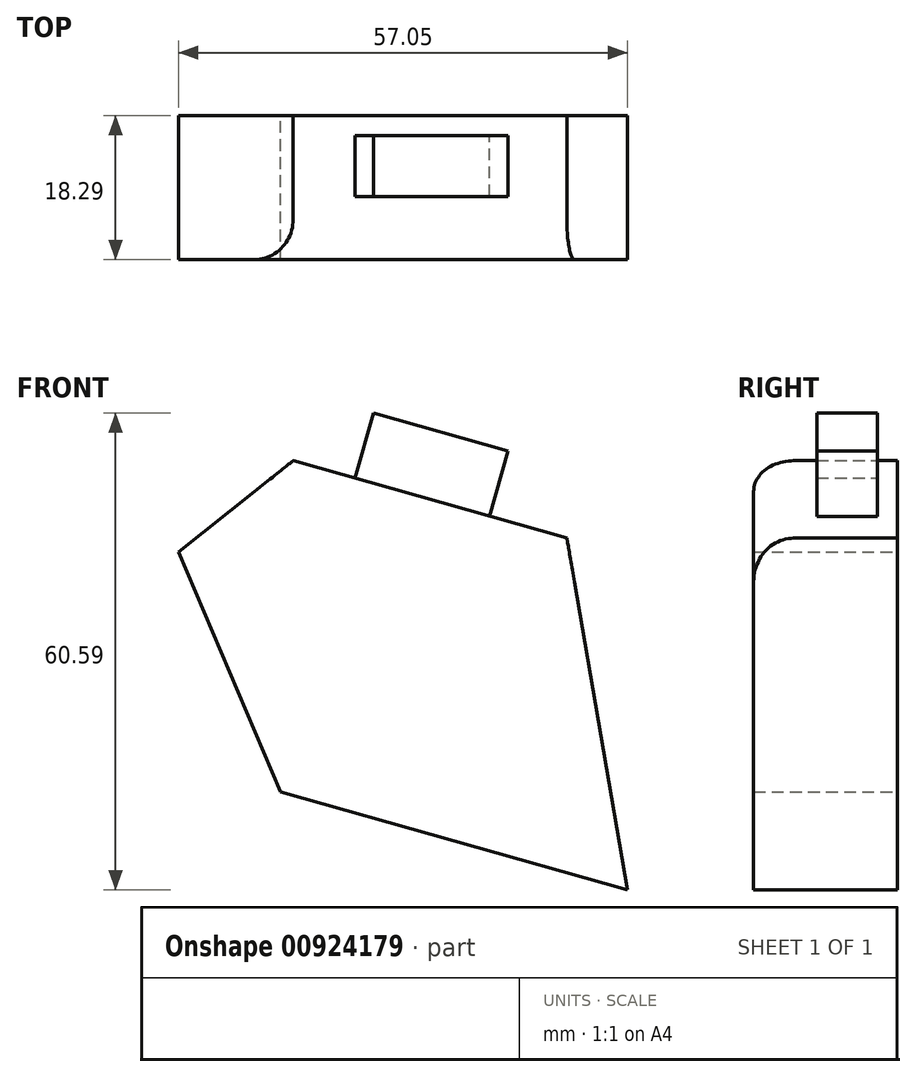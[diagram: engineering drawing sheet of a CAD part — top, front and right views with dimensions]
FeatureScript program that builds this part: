
annotation { "Feature Type Name" : "Feature", "Feature Type Description" : "" }
export const myFeature = defineFeature(function(context is Context, id is Id, definition is map)
    precondition{}
    {
        {
            var Q0;
            Q0=qCreatedBy(makeId("Front.planeOp"),FACE);
            var sketch = newSketch(context, id + "F0", { "sketchPlane" : qUnion([Q0])});
            skLineSegment(sketch, "E0", {"start": v(-28.41, 12.5) * mm, "end": v(-13.86, 24.09) * mm});
            skLineSegment(sketch, "E1", {"start": v(-13.86, 24.09) * mm, "end": v(20.9, 14.25) * mm});
            skLineSegment(sketch, "E2", {"start": v(20.9, 14.25) * mm, "end": v(28.64, -30.44) * mm});
            skLineSegment(sketch, "E3", {"start": v(28.64, -30.44) * mm, "end": v(-15.48, -17.96) * mm});
            skLineSegment(sketch, "E4", {"start": v(-15.48, -17.96) * mm, "end": v(-28.41, 12.5) * mm});
            skSolve(sketch);
        }
        {
            var Q0;
            Q0=makeQuery(id+"F0.imprint","IMPRINT",FACE,{"disambiguationData":[TD([[makeQuery(id+"F0.imprint","IMPRINT",EDGE,{"derivedFrom":sQuery(id+"F0.wireOp",EDGE,"E0")}),-1.0]])]});
            extrude(context, id + "F1", {"entities" : qUnion([Q0]), "depth" : 18.29 * mm, "offsetDistance" : 25.4 * mm});
        }
        {
            var Q0;
            Q0=makeQuery(id+"F1.opExtrude","SWEPT_FACE",FACE,{"disambiguationData":[OSD([sQuery(id+"F0.wireOp",EDGE,"E1")])]});
            var sketch = newSketch(context, id + "F2", { "sketchPlane" : qUnion([Q0])});
            skLineSegment(sketch, "E5.top", {"start": v(-11.74, -2.56) * mm, "end": v(6.04, -2.56) * mm});
            skLineSegment(sketch, "E5.left", {"start": v(-11.74, -10.27) * mm, "end": v(-11.74, -2.56) * mm});
            skLineSegment(sketch, "E5.right", {"start": v(6.04, -10.27) * mm, "end": v(6.04, -2.56) * mm});
            skLineSegment(sketch, "E6", {"start": v(-11.74, -10.27) * mm, "end": v(6.04, -10.27) * mm});
            skSolve(sketch);
        }
        {
            var Q0;
            Q0=makeQuery(id+"F2.imprint","IMPRINT",FACE,{"disambiguationData":[TD([[makeQuery(id+"F2.imprint","IMPRINT",EDGE,{"derivedFrom":sQuery(id+"F2.wireOp",EDGE,"E5.top")}),-1.0]])]});
            extrude(context, id + "F3", {"entities" : qUnion([Q0]), "operationType" : NewBodyOperationType.ADD, "depth" : 8.6 * mm, "offsetDistance" : 25.4 * mm});
        }
        {
            var Q0;
            Q0=makeQuery(id+"F1.opExtrude","CAP_EDGE",EDGE,{"disambiguationData":[OSD([sQuery(id+"F0.wireOp",EDGE,"E1")])],"isStart":false});
            fillet(context, id + "F4", {"entities" : qUnion([Q0]), "radius" : 5.08 * mm, "tangentPropagation" : true, "allowEdgeOverflow" : false});
        }
    });
